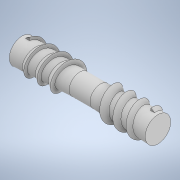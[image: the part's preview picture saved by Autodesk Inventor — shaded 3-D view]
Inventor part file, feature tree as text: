
AUTODESK INVENTOR PART (.ipt)
format: ipt  version: 2020 (Build 240168000, 168)  size: 236,032 bytes
history: native  units: mm
features: sketch x2, revolve x1, helix x1, mirror x1, projected_geometry x1
ambient origin geometry x8: Origin, YZ Plane, XZ Plane, XY Plane, X Axis, Y Axis, Z Axis, Center Point
bodies: Solid1 (feature_tree)
feature tree (6):
  revolve  "Revolution1"  [1 undecoded]
  helix  "Coil1"  [1 undecoded]
  mirror  "Mirror1"
  sketch  "Sketch1"  dims[d0=36.0mm d1=6.75mm d2=0.0mm]
  sketch  "Sketch2"  dims[d3=6.75mm d5=90.0deg d6=5.0mm d7=0.5mm d8=4.1mm d9=13.962634mm d10=2.4mm d11=7.0mm d12=24.5mm d13=10.0mm d14=0.0mm d15=90.0deg d16=90.0deg d17=0.0mm d18=0.0mm d19=5.5mm d20=5.5mm]
  projected_geometry  "Projected Loop1"
note: 2 required parameter values undecoded (feature->parameter linkage not recoverable at this tier; creation-order binding heuristic only, values carry confidence <= 0.55)